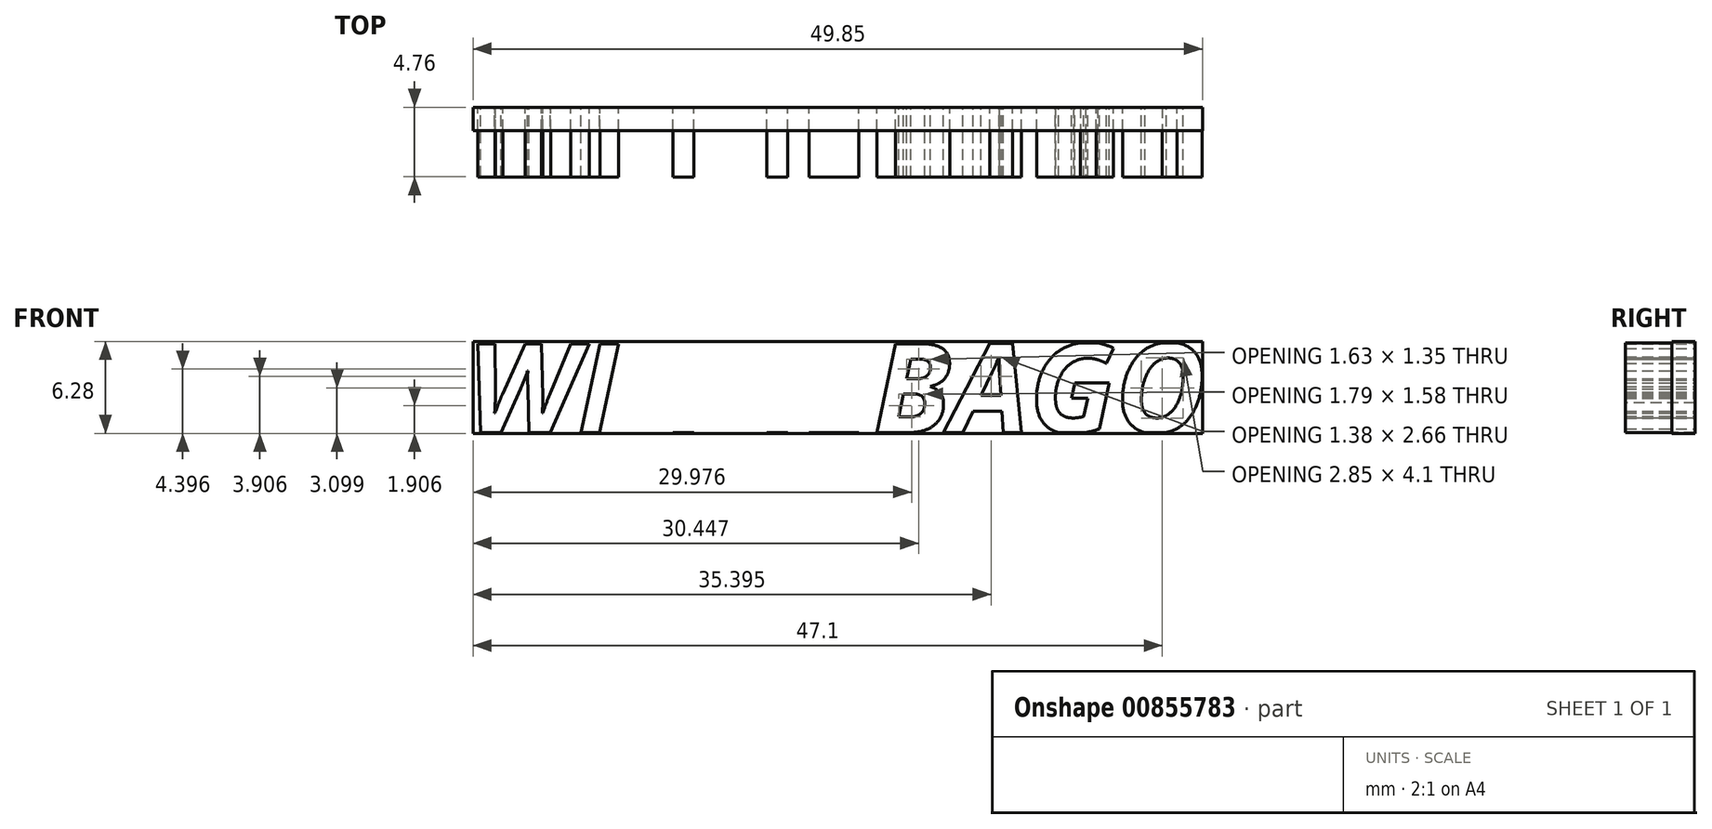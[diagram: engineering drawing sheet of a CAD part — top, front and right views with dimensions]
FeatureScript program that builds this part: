
annotation { "Feature Type Name" : "Feature", "Feature Type Description" : "" }
export const myFeature = defineFeature(function(context is Context, id is Id, definition is map)
    precondition{}
    {
        {
            var Q0;
            Q0=qCreatedBy(makeId("Front.planeOp"),FACE);
            var sketch = newSketch(context, id + "F0", { "sketchPlane" : qUnion([Q0])});
            skLineSegment(sketch, "E0.bottom", {"start": v(-29.34, 16.24) * mm, "end": v(21.46, 16.24) * mm});
            skLineSegment(sketch, "E0.top", {"start": v(-29.34, 10.1) * mm, "end": v(21.46, 10.1) * mm});
            skLineSegment(sketch, "E0.left", {"start": v(-29.34, 16.24) * mm, "end": v(-29.34, 10.1) * mm});
            skLineSegment(sketch, "E0.right", {"start": v(21.46, 16.24) * mm, "end": v(21.46, 10.1) * mm});
            skText(sketch, "E1", { "text": "WINNEBAGO", "fontName": "OpenSans-BoldItalic.ttf"});
            const initialGuessF0  = {"E1": [-0.02934, 0.0101, 1, 0, 0.00613]};
            skSetInitialGuess(sketch, initialGuessF0);
            skSolve(sketch);
        }
        {
            var Q0;
            Q0=makeQuery(id+"F0.imprint","IMPRINT",FACE,{"disambiguationData":[TD([[makeQuery(id+"F0.imprint","IMPRINT",EDGE,{"derivedFrom":sQuery(id+"F0.wireOp",EDGE,"E1.sketch_text.stroke-131")}),-1.0]])]});
            var Q1;
            Q1=makeQuery(id+"F0.imprint","IMPRINT",FACE,{"disambiguationData":[TD([[makeQuery(id+"F0.imprint","IMPRINT",EDGE,{"derivedFrom":sQuery(id+"F0.wireOp",EDGE,"E1.sketch_text.stroke-109")}),-1.0]])]});
            var Q2;
            Q2=makeQuery(id+"F0.imprint","IMPRINT",FACE,{"disambiguationData":[TD([[makeQuery(id+"F0.imprint","IMPRINT",EDGE,{"derivedFrom":sQuery(id+"F0.wireOp",EDGE,"E1.sketch_text.stroke-95")}),-1.0]])]});
            var Q3;
            Q3=makeQuery(id+"F0.imprint","IMPRINT",FACE,{"disambiguationData":[TD([[makeQuery(id+"F0.imprint","IMPRINT",EDGE,{"derivedFrom":sQuery(id+"F0.wireOp",EDGE,"E1.sketch_text.stroke-71")}),-1.0]])]});
            var Q4;
            Q4=makeQuery(id+"F0.imprint","IMPRINT",FACE,{"disambiguationData":[TD([[makeQuery(id+"F0.imprint","IMPRINT",EDGE,{"derivedFrom":sQuery(id+"F0.wireOp",EDGE,"E1.sketch_text.stroke-59")}),-1.0]])]});
            var Q5;
            Q5=makeQuery(id+"F0.imprint","IMPRINT",FACE,{"disambiguationData":[TD([[makeQuery(id+"F0.imprint","IMPRINT",EDGE,{"derivedFrom":sQuery(id+"F0.wireOp",EDGE,"E1.sketch_text.stroke-44")}),-1.0]])]});
            var Q6;
            Q6=makeQuery(id+"F0.imprint","IMPRINT",FACE,{"disambiguationData":[TD([[makeQuery(id+"F0.imprint","IMPRINT",EDGE,{"derivedFrom":sQuery(id+"F0.wireOp",EDGE,"E1.sketch_text.stroke-29")}),-1.0]])]});
            var Q7;
            Q7=makeQuery(id+"F0.imprint","IMPRINT",FACE,{"disambiguationData":[TD([[makeQuery(id+"F0.imprint","IMPRINT",EDGE,{"derivedFrom":sQuery(id+"F0.wireOp",EDGE,"E1.sketch_text.stroke-25")}),-1.0]])]});
            var Q8;
            Q8=makeQuery(id+"F0.imprint","IMPRINT",FACE,{"disambiguationData":[TD([[makeQuery(id+"F0.imprint","IMPRINT",EDGE,{"derivedFrom":sQuery(id+"F0.wireOp",EDGE,"E1.sketch_text.stroke-0")}),-1.0]])]});
            extrude(context, id + "F1", {"entities" : qUnion([Q0, Q1, Q2, Q3, Q4, Q5, Q6, Q7, Q8]), "depth" : 4.76 * mm, "offsetDistance" : 25.4 * mm});
        }
        {
            var Q0;
            Q0=qCreatedBy(makeId("Front.planeOp"),FACE);
            var sketch = newSketch(context, id + "F2", { "sketchPlane" : qUnion([Q0])});
            skLineSegment(sketch, "E2.bottom", {"start": v(-28.89, 16.33) * mm, "end": v(20.96, 16.33) * mm});
            skLineSegment(sketch, "E2.top", {"start": v(-28.89, 10.05) * mm, "end": v(20.96, 10.05) * mm});
            skLineSegment(sketch, "E2.left", {"start": v(-28.89, 16.33) * mm, "end": v(-28.89, 10.05) * mm});
            skLineSegment(sketch, "E2.right", {"start": v(20.96, 16.33) * mm, "end": v(20.96, 10.05) * mm});
            skSolve(sketch);
        }
        {
            var Q0;
            Q0 = qSketchRegion(id + "F2", true);
            extrude(context, id + "F3", {"entities" : qUnion([Q0]), "depth" : 1.59 * mm, "offsetDistance" : 25.4 * mm});
        }
    });
